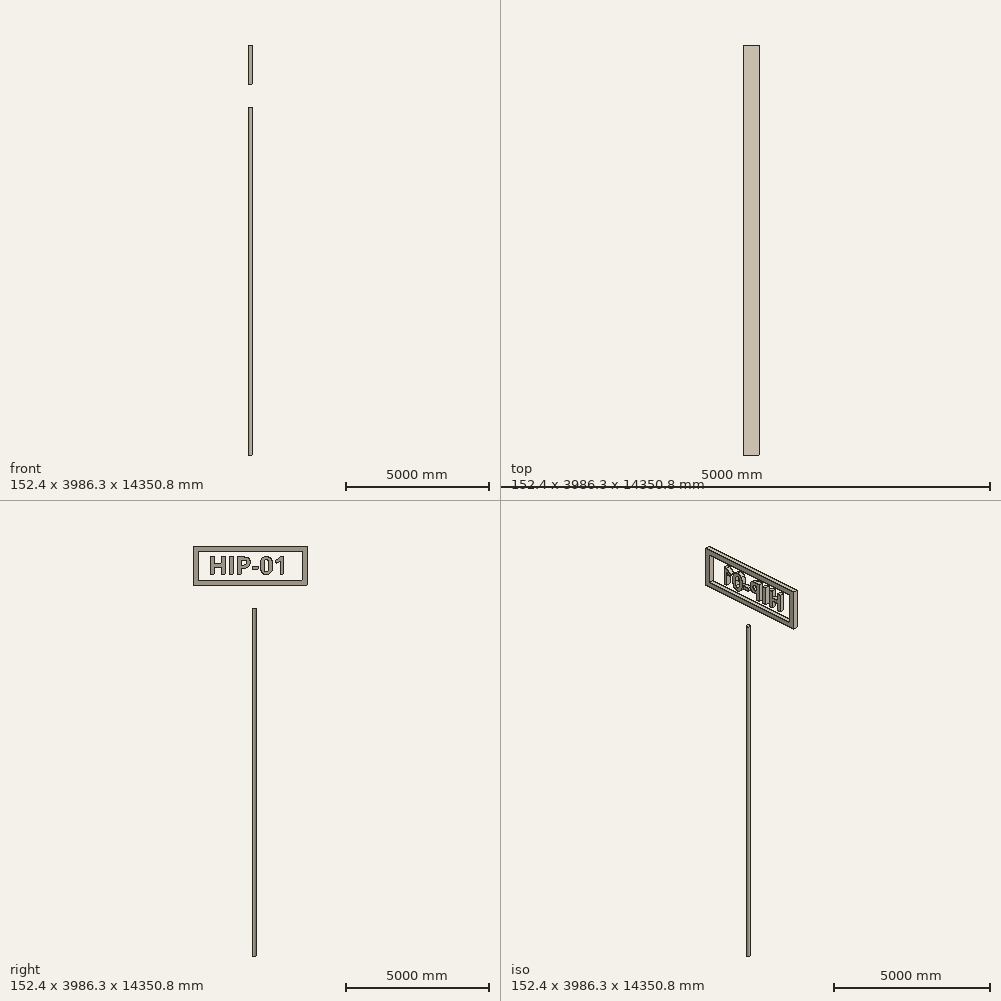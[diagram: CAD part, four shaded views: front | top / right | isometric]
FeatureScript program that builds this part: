
annotation { "Feature Type Name" : "Feature", "Feature Type Description" : "" }
export const myFeature = defineFeature(function(context is Context, id is Id, definition is map)
    precondition{}
    {
        {
            var Q0;
            Q0=qCreatedBy(makeId("Top.planeOp"),FACE);
            var sketch = newSketch(context, id + "F0", { "sketchPlane" : qUnion([Q0])});
            skCircle(sketch, "E0", {"center": v(0, 0) * mm, "radius": 76.2 * mm});
            skSolve(sketch);
        }
        {
            var Q0;
            Q0=qSketchRegion(id+"F0",true);
            extrude(context, id + "F1", {"entities" : qUnion([Q0]), "oppositeDirection" : true, "depth" : 12192 * mm});
        }
        {
            var Q0;
            Q0=qCreatedBy(makeId("Right.planeOp"),FACE);
            var sketch = newSketch(context, id + "F2", { "sketchPlane" : qUnion([Q0])});
            skText(sketch, "E1", { "text": "HIP-01", "fontName": "OpenSans-Bold.ttf"});
            const initialGuessF2  = {"E1": [-1.60948, 1.17133, 1, 0, 0.62756]};
            skSetInitialGuess(sketch, initialGuessF2);
            skSolve(sketch);
        }
        {
            var Q0;
            Q0=qCreatedBy(makeId("Right.planeOp"),FACE);
            var sketch = newSketch(context, id + "F3", { "sketchPlane" : qUnion([Q0])});
            skLineSegment(sketch, "E2.bottom", {"start": v(-1947.4, 1975.9) * mm, "end": v(1673.15, 1975.9) * mm});
            skLineSegment(sketch, "E2.top", {"start": v(-1947.4, 962.14) * mm, "end": v(1673.15, 962.14) * mm});
            skLineSegment(sketch, "E2.left", {"start": v(-1947.4, 1975.9) * mm, "end": v(-1947.4, 962.14) * mm});
            skLineSegment(sketch, "E2.right", {"start": v(1673.15, 1975.9) * mm, "end": v(1673.15, 962.14) * mm});
            skLineSegment(sketch, "E3.0", {"start": v(-2130.27, 2158.77) * mm, "end": v(1856.03, 2158.77) * mm});
            skLineSegment(sketch, "E3.1", {"start": v(-2130.27, 2158.77) * mm, "end": v(-2130.27, 779.26) * mm});
            skLineSegment(sketch, "E3.2", {"start": v(-2130.27, 779.26) * mm, "end": v(1856.03, 779.26) * mm});
            skLineSegment(sketch, "E3.3", {"start": v(1856.03, 2158.77) * mm, "end": v(1856.03, 779.26) * mm});
            skSolve(sketch);
        }
        {
            var Q0;
            Q0=makeQuery(id+"F3.imprint","IMPRINT",FACE,{"disambiguationData":[TD([[makeQuery(id+"F3.imprint","IMPRINT",EDGE,{"derivedFrom":sQuery(id+"F3.wireOp",EDGE,"E2.bottom")}),1.0]])]});
            extrude(context, id + "F4", {"entities" : qUnion([Q0]), "endBound" : BoundingType.SYMMETRIC, "depth" : 152.4 * mm});
        }
        {
            var Q0;
            Q0=qSketchRegion(id+"F2",true);
            extrude(context, id + "F5", {"entities" : qUnion([Q0]), "endBound" : BoundingType.SYMMETRIC, "depth" : 152.4 * mm});
        }
    });
